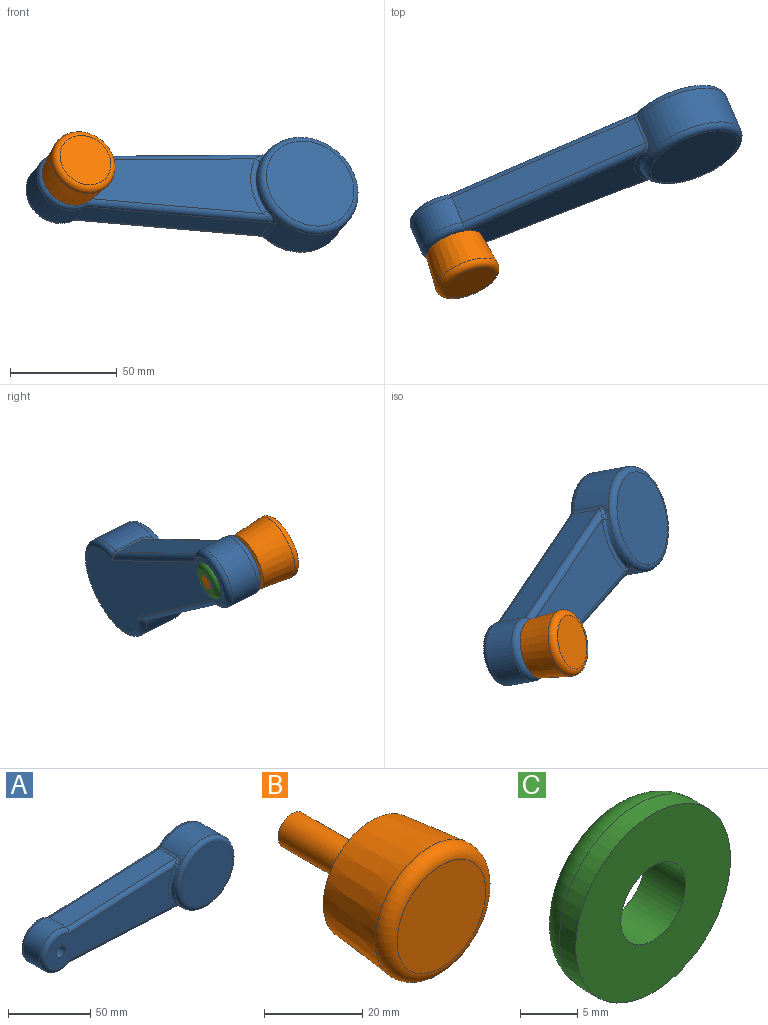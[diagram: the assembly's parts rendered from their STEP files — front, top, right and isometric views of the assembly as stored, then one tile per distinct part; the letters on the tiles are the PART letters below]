
ASSEMBLY  parts=3 mates=2
PART A: 25 faces, bbox 163.6x25x54.1 mm
  f0: cylinder r=25mm len=50mm, axis (0,1,0), area 2225.9mm2, adj f10,f15,f17,f18,f22,f23
  f1: plane 44x44mm, normal (0,-1,0), area 1520.5mm2, adj f15
  f2: plane 154.25x44mm, normal (0,1,0), area 4104.1mm2, adj f6,f8,f9,f10,f11
  f3: plane 93.56x14mm, normal (-0.05,0,1), area 1311.3mm2, adj f4,f8,f12,f17
  f4: cylinder r=15mm len=30mm, axis (0,1,0), area 885mm2, adj f3,f5,f9,f13
  f5: plane 93.56x14mm, normal (-0.05,0,-1), area 1311.3mm2, adj f4,f11,f14,f23
  f6: cylinder r=4mm len=20mm, axis (0,1,0), area 502.7mm2, adj f2,f7
  f7: plane 108.2x28.34mm, normal (0,-1,0), area 2402.1mm2, adj f6,f12,f13,f14,f20
  f8: cylinder r=3mm len=97.02mm, axis (-1,0,-0.05), area 449.2mm2, adj f2,f3,f9,f16
  f9: torus R=12mm, axis (0,-1,0), area 280.8mm2, adj f2,f4,f8,f11
  f10: torus R=22mm, axis (0,-1,0), area 534.4mm2, adj f0,f2,f16,f24
  f11: cylinder r=3mm len=97.02mm, axis (1,0,-0.05), area 449.2mm2, adj f2,f5,f9,f24
  f12: cylinder r=3mm len=94.66mm, axis (1,0,0.05), area 432.6mm2, adj f3,f7,f13,f18,f19
  f13: torus R=12mm, axis (0,-1,0), area 280.8mm2, adj f4,f7,f12,f14
  f14: cylinder r=3mm len=94.66mm, axis (-1,0,0.05), area 432.6mm2, adj f5,f7,f13,f21,f22
  f15: torus R=22mm, axis (0,-1,0), area 692.7mm2, adj f0,f1,f19,f20,f21
  f16: bspline ~3.69x3mm, area 3.7mm2, adj f8,f10,f17
  f17: bspline ~14x1.91mm, area 30.7mm2, adj f0,f3,f16,f18
  f18: bspline ~5.04x4.61mm, area 14.5mm2, adj f0,f12,f17,f19
  f19: bspline ~4.61x3.28mm, area 13.1mm2, adj f12,f15,f18,f20
  f20: bspline ~28.33x6.46mm, area 135.6mm2, adj f7,f15,f19,f21
  f21: bspline ~4.61x3.28mm, area 13.1mm2, adj f14,f15,f20,f22
  f22: bspline ~5x4.58mm, area 14.5mm2, adj f0,f14,f21,f23
  f23: bspline ~14x1.91mm, area 30.7mm2, adj f0,f5,f22,f24
  f24: bspline ~3.69x3mm, area 3.7mm2, adj f10,f11,f23
PART B: 6 faces, bbox 34.1x43x34.1 mm
  f0: cone r=14mm half-angle=6deg, axis (0,-1,0), area 1568.3mm2, adj f2,f3
  f1: plane 25.54x25.54mm, normal (0,-1,0), area 512.3mm2, adj f3
  f2: plane 28x28mm, normal (0,1,0), area 565.5mm2, adj f0,f4
  f3: torus R=12.77mm, axis (0,-1,0), area 465.8mm2, adj f0,f1
  f4: cylinder r=4mm len=23mm, axis (0,-1,0), area 578.1mm2, adj f2,f5
  f5: plane 8x8mm, normal (0,1,0), area 50.3mm2, adj f4
PART C: 5 faces, bbox 20.7x5.1x20.7 mm
  f0: cylinder r=4mm len=8mm, axis (0,-1,0), area 125.7mm2, adj f2,f3
  f1: cylinder r=9.57mm len=19.15mm, axis (0,-1,0), area 120.3mm2, adj f3,f4
  f2: plane 13.15x13.15mm, normal (0,1,0), area 85.5mm2, adj f0,f4
  f3: plane 19.15x19.15mm, normal (0,-1,0), area 237.7mm2, adj f0,f1
  f4: torus R=6.57mm, axis (0,-1,0), area 251.2mm2, adj f1,f2
PLACE A rot(axis=(-0.74,-0.08,0.66),33.7deg) t=(-35.23,-8.53,3.74)mm
PLACE B rot(axis=(-0.74,-0.08,0.66),33.7deg) t=(-34.8,-9.43,3.97)mm
PLACE C rot(axis=(-0.74,-0.08,0.66),33.7deg) t=(-34.07,-10.99,5)mm
MATE fastened C.f0 <-> B.f4  axis (-0.36,0.83,-0.42) through (-100.21,-33.21,5.46)mm
MATE revolute B.f4 <-> A.f6  axis (0.36,-0.83,0.42) through (-91.97,-52.38,15.14)mm
